# Revit family: P191568KX-085c_KOCE900H
name_source: partatom
category: Specialty Equipment
units: mm (PartAtom-declared; Revit-internal decimal feet)

## family parameters
Always vertical = Yes
Cut with Voids When Loaded = No
Enable Cutting in Views = No
Maintain Annotation Orientation = No
Part Type = Normal
Room Calculation Point = No
Round Connector Dimension = Use Diameter
Shared = No
Work Plane-Based = No

## types (1)
- KOCE900HSS
    Amps = 0 A
    Body Material = ARCAT - Metal - Steel - Stainless
    Clearance Material = ARCAT - Clearance
    Default Elevation = 0"
    Depth = 27 1/8"
    Description = Smart Oven+ 30" Combination Oven with Powered Attachments
Four intelligent+ combiné avec accessoires optimisés et fini PrintShield™, 30 po
    Display Panel Material = ARCAT - Glass - Black
    Door Material = ARCAT - Metal - Steel - Stainless
    Family Name = COOKING
    Feature 1 = Smart Oven+ Powered Attachments
Smart Oven+ Powered Attachments
    Feature 2 = Smart Oven+ Mobile App Connectivity
Smart Oven+ Mobile App Connectivity
    Feature 3 = +Grill Attachment
+Grill Attachment
    Glass Material = ARCAT - Glass - Tempered - Black
    Handle Material = ARCAT - Metal - Steel - Gray
    Height = 42 1/2"
    Installation-Fabrication = http://access.whirlpool.com Instruction&sku=KOCE900HSS&language=EN
http://access.whirlpool.com Instruction&sku=KOCE900HBS&language=EN
    Manufacturer = Kitchen Aid
    Model = KOCE900HSS
    Voltage = 0 V
    Width = 30"

## geometry (parser evidence)
native form markers: Sweep x6
no freeform markers — native parametric forms only
